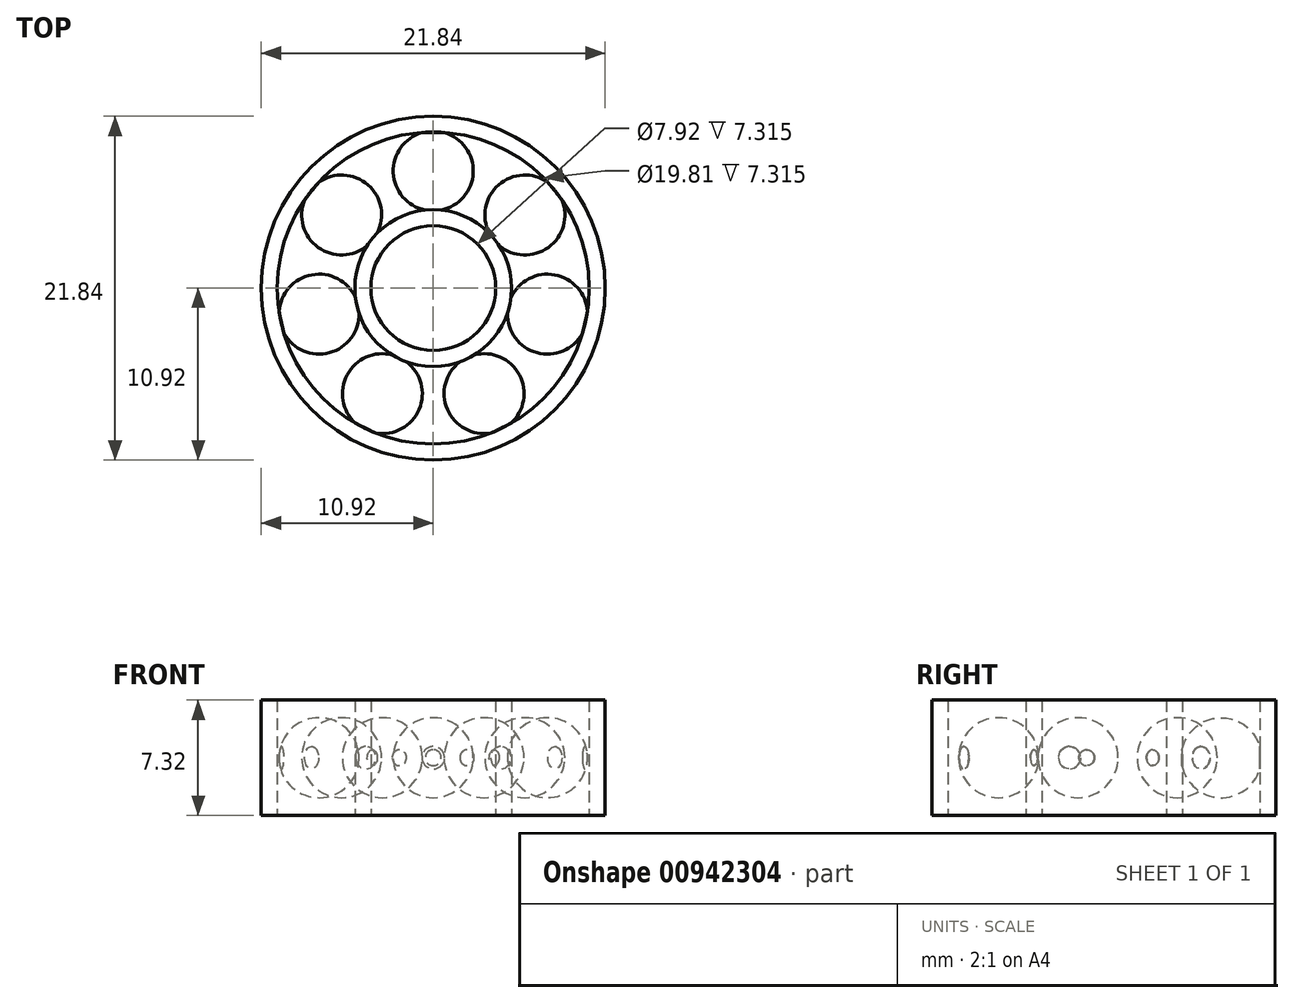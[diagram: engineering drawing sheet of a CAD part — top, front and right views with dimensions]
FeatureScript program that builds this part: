
annotation { "Feature Type Name" : "Feature", "Feature Type Description" : "" }
export const myFeature = defineFeature(function(context is Context, id is Id, definition is map)
    precondition{}
    {
        {
            var Q0;
            Q0=qCreatedBy(makeId("Top.planeOp"),FACE);
            var sketch = newSketch(context, id + "F0", { "sketchPlane" : qUnion([Q0])});
            skCircle(sketch, "E0", {"center": v(0, 0) * mm, "radius": 3.96 * mm});
            skCircle(sketch, "E1", {"center": v(0, 0) * mm, "radius": 4.98 * mm});
            skCircle(sketch, "E2", {"center": v(0, 0) * mm, "radius": 10.92 * mm});
            skCircle(sketch, "E3", {"center": v(0, 0) * mm, "radius": 9.9 * mm});
            skLineSegment(sketch, "E4", {"start": v(0, 9.9) * mm, "end": v(0, 4.98) * mm});
            skCircle(sketch, "E5", {"center": v(0, 7.44) * mm, "radius": 2.54 * mm});
            skSolve(sketch);
        }
        {
            var Q0;
            Q0=makeQuery(id+"F0.imprint","IMPRINT",FACE,{"disambiguationData":[TD([[makeQuery(id+"F0.imprint","IMPRINT",EDGE,{"derivedFrom":sQuery(id+"F0.wireOp",EDGE,"E2")}),1.0]])]});
            var Q1;
            Q1=makeQuery(id+"F0.imprint","IMPRINT",FACE,{"disambiguationData":[TD([[makeQuery(id+"F0.imprint","IMPRINT",EDGE,{"derivedFrom":sQuery(id+"F0.wireOp",EDGE,"E0")}),-1.0]])]});
            var Q2;
            {var subQ0=sQuery(id+"F0.wireOp",EDGE,"E3");var subQ1=makeQuery(id+"F0.imprint","INTERSECT",VERTEX,{"derivedFrom":[subQ0,sQuery(id+"F0.wireOp",EDGE,"E4")]});Q2=makeQuery(id+"F0.imprint","IMPRINT",FACE,{"disambiguationData":[TD([[makeQuery(id+"F0.imprint","IMPRINT",EDGE,{"disambiguationData":[TD([[subQ1,1.0]])],"derivedFrom":subQ0}),-1.0]])]});}
            var Q3;
            {var subQ0=sQuery(id+"F0.wireOp",EDGE,"E1");var subQ1=makeQuery(id+"F0.imprint","INTERSECT",VERTEX,{"derivedFrom":[subQ0,sQuery(id+"F0.wireOp",EDGE,"E4")]});Q3=makeQuery(id+"F0.imprint","IMPRINT",FACE,{"disambiguationData":[TD([[makeQuery(id+"F0.imprint","IMPRINT",EDGE,{"disambiguationData":[TD([[subQ1,1.0]])],"derivedFrom":subQ0}),1.0]])]});}
            extrude(context, id + "F1", {"entities" : qUnion([Q0, Q1, Q2, Q3]), "endBound" : BoundingType.SYMMETRIC, "depth" : 7.32 * mm, "offsetDistance" : 25.4 * mm});
        }
        {
            var Q0;
            {var subQ0=sQuery(id+"F0.wireOp",EDGE,"E4");Q0=makeQuery(id+"F0.imprint","IMPRINT",FACE,{"disambiguationData":[TD([[makeQuery(id+"F0.imprint","IMPRINT",EDGE,{"derivedFrom":subQ0}),1.0]])]});}
            var Q1;
            Q1=sQuery(id+"F0.wireOp",EDGE,"E4");
            revolve(context, id + "F2", {"surfaceOperationType" : NewSurfaceOperationType.NEW, "entities" : qUnion([Q0]), "axis" : qUnion([Q1]), "revolveType" : RevolveType.FULL});
        }
        {
            var Q0;
            Q0=makeQuery(id+"F2.opRevolve","SWEPT_BODY",BODY,{"disambiguationData":[OSD([sQuery(id+"F0.wireOp",EDGE,"E4"),sQuery(id+"F0.wireOp",EDGE,"E5")])]});
            var Q1;
            Q1=makeQuery(id+"F1.opExtrude","CAP_EDGE",EDGE,{"disambiguationData":[OSD([sQuery(id+"F0.wireOp",EDGE,"E3")])],"isStart":true});
            circularPattern(context, id + "F3", {"entities" : qUnion([Q0]), "axis" : qUnion([Q1]), "angle" : 360 * degree, "instanceCount" : 7, "equalSpace" : true});
        }
    });
